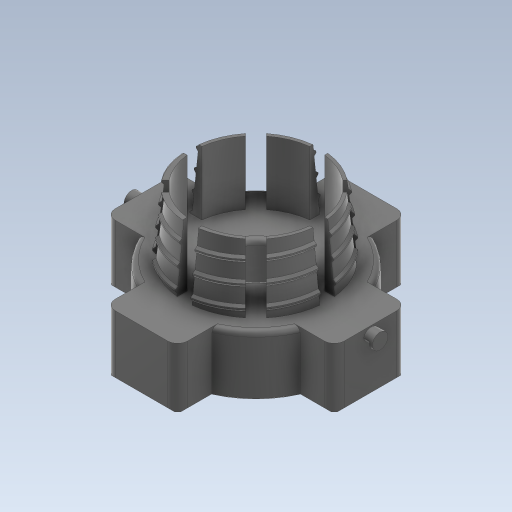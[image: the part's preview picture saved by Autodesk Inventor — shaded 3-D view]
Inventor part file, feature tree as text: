
AUTODESK INVENTOR PART (.ipt)
format: ipt  version: 2023 (Build 270158000, 158)  size: 1,051,648 bytes
history: native  units: mm
features: sketch x7, extrude x6, fillet x3, other x2, helix x2, draft x1, direct_edit x1, hole x1, pattern_circular x1, chamfer x1, projected_geometry x1
ambient origin geometry x8: Origin, YZ Plane, XZ Plane, XY Plane, X Axis, Y Axis, Z Axis, Center Point
bodies: Solid1 (feature_tree)
feature tree (26):
  other  "Slider V8 (4mm pitch)"
  extrude  "Extrusion1"  Depth=26.5mm
  draft  "FaceDraft1"
  sketch  "Sketch2"  dims[d34=0.0mm d35=0.0mm]
  helix  "Coil3"  [1 undecoded]
  helix  "Coil4"  [1 undecoded]
  direct_edit  "Direct Edit2"
  extrude  "Extrusion2"  Depth=12.0mm TaperAngle=0.0deg
  sketch  "Sketch4"  dims[d56=8.726646mm d62=4.0mm d63=13.0mm d64=10.0mm d65=1.047198mm]
  extrude  "Extrusion3"  Depth=10.0mm
  extrude  "Extrusion8"  TaperAngle=90.0deg  [1 undecoded]
  hole  "Hole1"  [1 undecoded]
  sketch  "Sketch9"  dims[d83=3.0mm d84=1.5mm d85=1.5mm d86=0.0mm d87=0.0mm d91=3.0mm d92=3.0mm d93=1.5mm d94=1.5mm d95=5.3mm d96=6.0mm d97=10.0mm d98=10.0mm d99=90.0deg d100=8.0mm d101=20.594885mm d108=35.6mm d110=3.15mm d113=1.575mm d114=7.45mm d115=2.35mm d117=3.6mm d118=0.0mm d119=1.2mm d120=0.0mm d121=20.0mm d122=360.0deg d126=1.0mm d129=0.3mm d130=2.0mm d131=45.0deg d133=14.65mm d134=14.65mm d137=23.15mm d138=46.3mm d139=46.3mm d142=1.0mm d143=2.0mm d109=0.5mm d111=0.5mm d112=0.872665mm]
  extrude  "Extrusion11"  Depth=2.0mm
  extrude  "Extrusion12"  Depth=2.0mm
  pattern_circular  "Circular Pattern1"  [2 undecoded]
  fillet  "Fillet4"  Radius=3.0mm
  chamfer  "Chamfer2"  Distance=3.0mm
  fillet  "Fillet7"  Radius=1.5mm
  fillet  "Fillet8"  Radius=1.5mm
  sketch  "Sketch1"  dims[d0=25.0mm d1=26.5mm d2=12.875mm d3=0.0mm d4=1.047198mm]
  sketch  "Sketch3"  dims[d36=7.325mm d37=7.0mm d38=7.325mm d39=0.0mm d40=7.0mm d41=28.73603mm d42=12.0mm d43=0.0mm]
  sketch  "Sketch5"  dims[d66=90.0deg d67=90.0deg d68=0.0mm d69=0.0mm d70=4.0mm d71=3.0mm d72=10.0mm d73=-1.047198mm d74=90.0deg d75=90.0deg d76=0.0mm d77=0.0mm]
  sketch  "Sketch7"  dims[d79=-0.127mm d82=3.0mm]
  projected_geometry  "Projected Loop1"
  other  "Size2"
note: 6 required parameter values undecoded (feature->parameter linkage not recoverable at this tier; creation-order binding heuristic only, values carry confidence <= 0.55)
